# Revit family: xxxShower_Base-American_Standard-Studio-2946.ST_Series
name_source: partatom
category: Plumbing Fixtures
units: mm (PartAtom-declared; Revit-internal decimal feet)

## family parameters
Always vertical = No
Cut with Voids When Loaded = No
OmniClass Number = 23.45.05.14.17
OmniClass Title = Showers
Part Type = Normal
Room Calculation Point = No
Round Connector Dimension = Use Diameter
Shared = Yes
Work Plane-Based = Yes

## types (2) — shared parameters
2946SW.011 Shower Walls = No
Assembly Code = D2010710
CSA B45.5-11 / IAPMO Z124-2011 = Yes
CW Connection = No
CWFU = 3
Default Elevation = 0"
Finish = High Gloss Acrylic-American Standard-011-Arctic White
Finish-Drain Plate = Metal-American Standard-Stainless Steel
HW Connection = No
HWFU = 3
Height = 5"
Installation Instruction Link = https://americanstandard.box.com
Installation Type = Floor Mounted
Length = 60"
Manufacturer = American Standard
Material = High Gloss Acrylic-American Standard-011-Arctic White
Product Documentation Link = https://americanstandard.box.com
Product Page URL = https://www.americanstandard-us.com
Revised Date = 03/20/2022
URL = https://www.americanstandard-us.com
Vent Connection = No
WFU = 4
Warranty Information = Limited Lifetime Warranty
Waste Connection = Yes
Waste Connection Diameter = 2"
Width = 32 1/4"
cUPC Compliant = Yes

## per-type parameters (varying)
| type | Description | Drain Location |
| 2946.STR | Studio 60x32 inch Single Threshold Shower base with Right-hand Outlet | 52" |
| 2946.STL | Studio 60x32 inch Single Threshold Shower base with Left-hand Outlet | 8" |

note: column(s) folded — value = type name in every type: Model

## geometry (parser evidence)
native form markers: Sweep x1
no freeform markers — native parametric forms only
